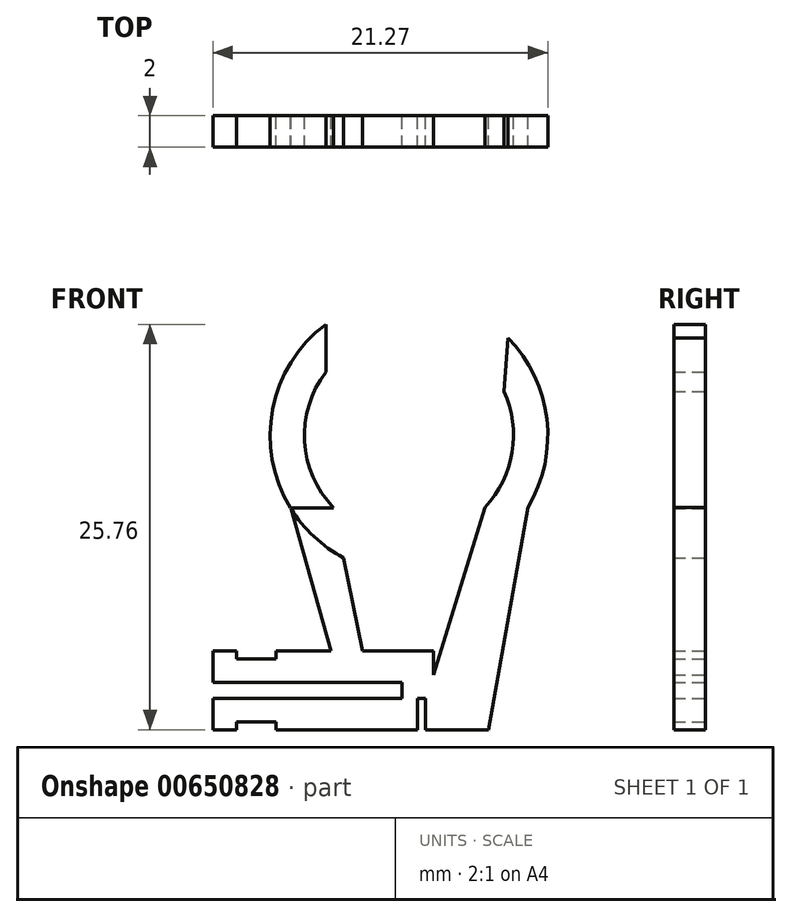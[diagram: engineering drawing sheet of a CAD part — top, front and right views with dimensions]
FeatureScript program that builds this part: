
annotation { "Feature Type Name" : "Feature", "Feature Type Description" : "" }
export const myFeature = defineFeature(function(context is Context, id is Id, definition is map)
    precondition{}
    {
        {
            var Q0;
            Q0=qCreatedBy(makeId("Front.planeOp"),FACE);
            var sketch = newSketch(context, id + "F0", { "sketchPlane" : qUnion([Q0])});
            skLineSegment(sketch, "E0", {"start": v(-45.6, 16.37) * mm, "end": v(-45.6, 14.37) * mm});
            skLineSegment(sketch, "E1", {"start": v(-45.6, 14.37) * mm, "end": v(-33.6, 14.37) * mm});
            skLineSegment(sketch, "E2", {"start": v(-33.6, 14.37) * mm, "end": v(-33.6, 13.37) * mm});
            skLineSegment(sketch, "E3", {"start": v(-33.6, 13.37) * mm, "end": v(-45.6, 13.37) * mm});
            skLineSegment(sketch, "E4", {"start": v(-45.6, 13.37) * mm, "end": v(-45.6, 11.37) * mm});
            skLineSegment(sketch, "E5", {"start": v(-45.6, 11.37) * mm, "end": v(-44.1, 11.37) * mm});
            skLineSegment(sketch, "E6", {"start": v(-44.1, 11.37) * mm, "end": v(-44.1, 11.87) * mm});
            skLineSegment(sketch, "E7", {"start": v(-44.1, 11.87) * mm, "end": v(-41.6, 11.87) * mm});
            skLineSegment(sketch, "E8", {"start": v(-41.6, 11.87) * mm, "end": v(-41.6, 11.37) * mm});
            skLineSegment(sketch, "E9", {"start": v(-41.6, 11.37) * mm, "end": v(-32.6, 11.37) * mm});
            skLineSegment(sketch, "E10", {"start": v(-32.6, 11.37) * mm, "end": v(-32.6, 13.37) * mm});
            skLineSegment(sketch, "E11", {"start": v(-32.6, 13.37) * mm, "end": v(-32.1, 13.37) * mm});
            skLineSegment(sketch, "E12", {"start": v(-32.1, 13.37) * mm, "end": v(-32.1, 11.37) * mm});
            skLineSegment(sketch, "E13", {"start": v(-32.1, 11.37) * mm, "end": v(-28.1, 11.37) * mm});
            skLineSegment(sketch, "E14", {"start": v(-28.1, 11.37) * mm, "end": v(-25.6, 25.58) * mm});
            skLineSegment(sketch, "E15", {"start": v(-45.6, 16.37) * mm, "end": v(-44.1, 16.37) * mm});
            skLineSegment(sketch, "E16", {"start": v(-44.1, 16.37) * mm, "end": v(-44.1, 15.87) * mm});
            skLineSegment(sketch, "E17", {"start": v(-44.1, 15.87) * mm, "end": v(-41.6, 15.87) * mm});
            skLineSegment(sketch, "E18", {"start": v(-41.6, 15.87) * mm, "end": v(-41.6, 16.37) * mm});
            skLineSegment(sketch, "E19", {"start": v(-41.6, 16.37) * mm, "end": v(-38.1, 16.37) * mm});
            skLineSegment(sketch, "E20", {"start": v(-38.1, 16.37) * mm, "end": v(-41.6, 28.81) * mm});
            skPoint(sketch, "E21", {"position": v(-40.66, 25.45) * mm});
            skLineSegment(sketch, "E22", {"start": v(-41.6, 28.81) * mm, "end": v(-40.66, 25.45) * mm});
            skCircle(sketch, "E23", {"center": v(-33.16, 30.07) * mm, "radius": 6.64 * mm});
            skCircle(sketch, "E24", {"center": v(-33.16, 30.07) * mm, "radius": 8.82 * mm});
            skLineSegment(sketch, "E25", {"start": v(-25.61, 25.5) * mm, "end": v(-40.67, 25.46) * mm});
            skLineSegment(sketch, "E26", {"start": v(-26.88, 36.26) * mm, "end": v(-38.44, 37.13) * mm});
            skLineSegment(sketch, "E27", {"start": v(-38.1, 16.37) * mm, "end": v(-33.6, 16.37) * mm});
            skLineSegment(sketch, "E28", {"start": v(-33.6, 16.37) * mm, "end": v(-31.6, 16.37) * mm});
            skLineSegment(sketch, "E29", {"start": v(-31.6, 16.37) * mm, "end": v(-31.6, 14.87) * mm});
            skLineSegment(sketch, "E30", {"start": v(-31.6, 14.87) * mm, "end": v(-28.34, 25.5) * mm});
            skLineSegment(sketch, "E31", {"start": v(-31.6, 16.37) * mm, "end": v(-36.1, 16.37) * mm});
            skLineSegment(sketch, "E32", {"start": v(-36.1, 16.37) * mm, "end": v(-37.94, 25.47) * mm});
            skLineSegment(sketch, "E33", {"start": v(-38.44, 37.13) * mm, "end": v(-38.44, 34.1) * mm});
            skLineSegment(sketch, "E34", {"start": v(-26.88, 36.26) * mm, "end": v(-27.13, 32.87) * mm});
            skSolve(sketch);
        }
        {
            var Q0;
            {var subQ6=sQuery(id+"F0.wireOp",EDGE,"E33");Q0=makeQuery(id+"F0.imprint","IMPRINT",FACE,{"disambiguationData":[TD([[makeQuery(id+"F0.imprint","IMPRINT",EDGE,{"derivedFrom":subQ6}),-1.0]])]});}
            var Q1;
            {var subQ3=sQuery(id+"F0.wireOp",EDGE,"E34");Q1=makeQuery(id+"F0.imprint","IMPRINT",FACE,{"disambiguationData":[TD([[makeQuery(id+"F0.imprint","IMPRINT",EDGE,{"derivedFrom":subQ3}),1.0]])]});}
            var Q2;
            {var subQ1=sQuery(id+"F0.wireOp",EDGE,"E24");var subQ3=sQuery(id+"F0.wireOp",EDGE,"E30");var subQ4=makeQuery(id+"F0.imprint","INTERSECT",VERTEX,{"derivedFrom":[subQ1,subQ3]});Q2=makeQuery(id+"F0.imprint","IMPRINT",FACE,{"disambiguationData":[TD([[makeQuery(id+"F0.imprint","IMPRINT",EDGE,{"disambiguationData":[TD([[subQ4,-1.0]])],"derivedFrom":subQ1}),1.0]])]});}
            var Q3;
            {var subQ3=sQuery(id+"F0.wireOp",EDGE,"E22");var subQ5=sQuery(id+"F0.wireOp",EDGE,"E20");var subQ6=makeQuery(id+"F0.imprint","INTERSECT",VERTEX,{"derivedFrom":[subQ5,subQ3]});Q3=makeQuery(id+"F0.imprint","IMPRINT",FACE,{"disambiguationData":[TD([[makeQuery(id+"F0.imprint","IMPRINT",EDGE,{"disambiguationData":[TD([[subQ6,1.0]])],"derivedFrom":subQ5}),-1.0]])]});}
            var Q4;
            {var subQ0=sQuery(id+"F0.wireOp",EDGE,"E27");Q4=makeQuery(id+"F0.imprint","IMPRINT",FACE,{"disambiguationData":[TD([[makeQuery(id+"F0.imprint","IMPRINT",EDGE,{"derivedFrom":subQ0}),1.0]])]});}
            var Q5;
            Q5=makeQuery(id+"F0.imprint","IMPRINT",FACE,{"disambiguationData":[TD([[makeQuery(id+"F0.imprint","IMPRINT",EDGE,{"derivedFrom":sQuery(id+"F0.wireOp",EDGE,"E0")}),1.0]])]});
            extrude(context, id + "F1", {"entities" : qUnion([Q0, Q1, Q2, Q3, Q4, Q5]), "depth" : 2 * mm, "offsetDistance" : 25 * mm});
        }
    });
